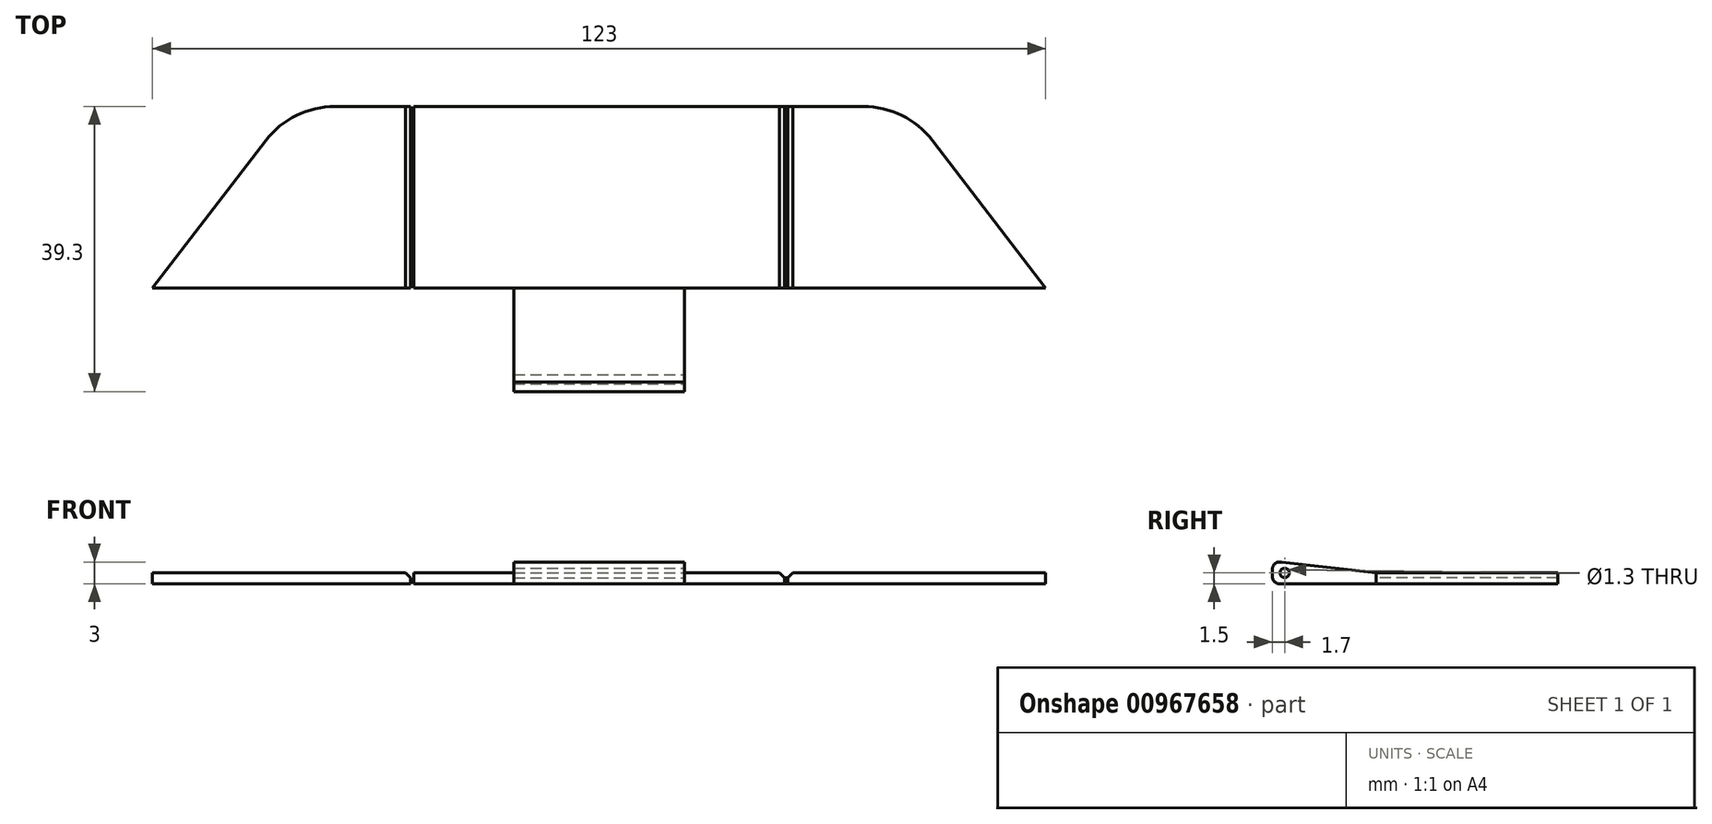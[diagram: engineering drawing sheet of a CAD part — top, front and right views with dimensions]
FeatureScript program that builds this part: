
annotation { "Feature Type Name" : "Feature", "Feature Type Description" : "" }
export const myFeature = defineFeature(function(context is Context, id is Id, definition is map)
    precondition{}
    {
        {
            var Q0;
            Q0=qCreatedBy(makeId("Top.planeOp"),FACE);
            var sketch = newSketch(context, id + "F0", { "sketchPlane" : qUnion([Q0])});
            skLineSegment(sketch, "E0.bottom", {"start": v(-11.75, -19.65) * mm, "end": v(11.75, -19.65) * mm});
            skLineSegment(sketch, "E0.top", {"start": v(-11.75, 19.65) * mm, "end": v(11.75, 19.65) * mm});
            skLineSegment(sketch, "E0.left", {"start": v(-11.75, -19.65) * mm, "end": v(-11.75, -5.35) * mm});
            skLineSegment(sketch, "E0.right", {"start": v(11.75, -19.65) * mm, "end": v(11.75, -5.35) * mm});
            skPoint(sketch, "E0.middle", {"position": v(0, 0) * mm});
            skLineSegment(sketch, "E1", {"start": v(-17.83, -17.95) * mm, "end": v(20.68, -17.95) * mm, "construction": true});
            skLineSegment(sketch, "E2", {"start": v(-16.64, -5.35) * mm, "end": v(-11.75, -5.35) * mm, "construction": true});
            skLineSegment(sketch, "E3.bottom", {"start": v(-25.5, -5.35) * mm, "end": v(-11.75, -5.35) * mm});
            skLineSegment(sketch, "E3.top", {"start": v(-25.5, 19.65) * mm, "end": v(25.5, 19.65) * mm});
            skLineSegment(sketch, "E3.left", {"start": v(-25.5, -5.35) * mm, "end": v(-25.5, 19.65) * mm});
            skLineSegment(sketch, "E3.right", {"start": v(25.5, -5.35) * mm, "end": v(25.5, 19.65) * mm});
            skPoint(sketch, "E3.middle", {"position": v(0, 7.15) * mm});
            skLineSegment(sketch, "E4.trimOffspring", {"start": v(11.75, -5.35) * mm, "end": v(19.97, -5.35) * mm, "construction": true});
            skLineSegment(sketch, "E5.trimOffspring", {"start": v(11.75, -5.35) * mm, "end": v(25.5, -5.35) * mm});
            skPoint(sketch, "E6.oppositeSnap0", {"position": v(-18.62, -5.35) * mm});
            skLineSegment(sketch, "E6.bottom", {"start": v(-25.5, 19.65) * mm, "end": v(-36.38, 19.65) * mm});
            skLineSegment(sketch, "E6.top", {"start": v(-25.5, -5.35) * mm, "end": v(-61.5, -5.35) * mm});
            skLineSegment(sketch, "E6.left", {"start": v(-25.5, 19.65) * mm, "end": v(-25.5, -5.35) * mm});
            skLineSegment(sketch, "E7", {"start": v(-26, 19.65) * mm, "end": v(-26, -5.35) * mm});
            skLineSegment(sketch, "E8", {"start": v(-45.9, 14.96) * mm, "end": v(-61.5, -5.35) * mm});
            skPoint(sketch, "E9.visualSharp", {"position": v(-42.3, 19.65) * mm});
            skArc(sketch, "E9.filletArc", {"start": v(-36.38, 19.65) * mm, "mid": v(-41.68, 18.41) * mm, "end": v(-45.9, 14.96) * mm});
            skLineSegment(sketch, "E10.MirrorCS", {"start": v(26, 19.65) * mm, "end": v(26, -5.35) * mm});
            skLineSegment(sketch, "E11.MirrorCS", {"start": v(25.5, 19.65) * mm, "end": v(36.38, 19.65) * mm});
            skArc(sketch, "E12.MirrorCS", {"start": v(36.38, 19.65) * mm, "mid": v(41.68, 18.41) * mm, "end": v(45.9, 14.96) * mm});
            skLineSegment(sketch, "E13.MirrorCS", {"start": v(45.9, 14.96) * mm, "end": v(61.5, -5.35) * mm});
            skLineSegment(sketch, "E14.MirrorCS", {"start": v(25.5, -5.35) * mm, "end": v(61.5, -5.35) * mm});
            skLineSegment(sketch, "E15", {"start": v(-11.75, -5.35) * mm, "end": v(11.75, -5.35) * mm});
            skSolve(sketch);
        }
        {
            var Q0;
            Q0=makeQuery(id+"F0.imprint","IMPRINT",FACE,{"disambiguationData":[TD([[makeQuery(id+"F0.imprint","IMPRINT",EDGE,{"derivedFrom":sQuery(id+"F0.wireOp",EDGE,"E0.bottom")}),1.0]])]});
            extrude(context, id + "F1", {"entities" : qUnion([Q0]), "depth" : 3 * mm, "offsetDistance" : 25 * mm});
        }
        {
            var Q0;
            Q0=makeQuery(id+"F1.opExtrude","SWEPT_FACE",FACE,{"disambiguationData":[OSD([sQuery(id+"F0.wireOp",EDGE,"E0.right")])]});
            var sketch = newSketch(context, id + "F2", { "sketchPlane" : qUnion([Q0])});
            skCircle(sketch, "E16", {"center": v(-17.95, 1.5) * mm, "radius": 0.65 * mm});
            skLineSegment(sketch, "E17", {"start": v(-16, 3) * mm, "end": v(-19.65, 0) * mm, "construction": true});
            skLineSegment(sketch, "E18", {"start": v(-16, 0) * mm, "end": v(-19.65, 3) * mm, "construction": true});
            skLineSegment(sketch, "E19", {"start": v(-17.82, 1.5) * mm, "end": v(-18.92, 1.5) * mm, "construction": true});
            skSolve(sketch);
        }
        {
            var Q0;
            Q0 = qSketchRegion(id + "F2", true);
            extrude(context, id + "F3", {"entities" : qUnion([Q0]), "operationType" : NewBodyOperationType.REMOVE, "oppositeDirection" : true, "depth" : 25 * mm, "offsetDistance" : 25 * mm});
        }
        {
            var Q0;
            Q0=makeQuery(id+"F1.opExtrude","CAP_EDGE",EDGE,{"disambiguationData":[OSD([sQuery(id+"F0.wireOp",EDGE,"E0.bottom")])],"isStart":false});
            var Q1;
            Q1=makeQuery(id+"F1.opExtrude","CAP_EDGE",EDGE,{"disambiguationData":[OSD([sQuery(id+"F0.wireOp",EDGE,"E0.bottom")])],"isStart":true});
            fillet(context, id + "F4", {"entities" : qUnion([Q0, Q1]), "radius" : 1 * mm, "tangentPropagation" : true, "allowEdgeOverflow" : false});
        }
        {
            var Q0;
            {var subQ0=sQuery(id+"F0.wireOp",EDGE,"E7");Q0=makeQuery(id+"F0.imprint","IMPRINT",FACE,{"disambiguationData":[TD([[makeQuery(id+"F0.imprint","IMPRINT",EDGE,{"derivedFrom":subQ0}),-1.0]])]});}
            var Q1;
            {var subQ3=sQuery(id+"F0.wireOp",EDGE,"E10.MirrorCS");Q1=makeQuery(id+"F0.imprint","IMPRINT",FACE,{"disambiguationData":[TD([[makeQuery(id+"F0.imprint","IMPRINT",EDGE,{"derivedFrom":subQ3}),1.0]])]});}
            extrude(context, id + "F5", {"entities" : qUnion([Q0, Q1]), "depth" : 1.5 * mm, "offsetDistance" : 25 * mm});
        }
        {
            var Q0;
            {var subQ0=sQuery(id+"F0.wireOp",EDGE,"E6.left");Q0=makeQuery(id+"F0.imprint","IMPRINT",FACE,{"disambiguationData":[TD([[makeQuery(id+"F0.imprint","IMPRINT",EDGE,{"derivedFrom":subQ0}),-1.0]])]});}
            var Q1;
            {var subQ0=sQuery(id+"F0.wireOp",EDGE,"E3.right");Q1=makeQuery(id+"F0.imprint","IMPRINT",FACE,{"disambiguationData":[TD([[makeQuery(id+"F0.imprint","IMPRINT",EDGE,{"derivedFrom":subQ0}),-1.0]])]});}
            extrude(context, id + "F6", {"entities" : qUnion([Q0, Q1]), "depth" : .8 * mm, "offsetDistance" : 25 * mm});
        }
        {
            var Q0;
            Q0=makeQuery(id+"F0.imprint","IMPRINT",FACE,{"disambiguationData":[TD([[makeQuery(id+"F0.imprint","IMPRINT",EDGE,{"derivedFrom":sQuery(id+"F0.wireOp",EDGE,"E3.bottom")}),1.0]])]});
            extrude(context, id + "F7", {"entities" : qUnion([Q0]), "depth" : 1.5 * mm, "offsetDistance" : 25 * mm});
        }
        {
            var Q0;
            Q0=makeQuery(id+"F7.opExtrude","CAP_EDGE",EDGE,{"disambiguationData":[OSD([sQuery(id+"F0.wireOp",EDGE,"E6.left")])],"isStart":false});
            var Q1;
            Q1=makeQuery(id+"F5.opExtrude","CAP_EDGE",EDGE,{"disambiguationData":[OSD([sQuery(id+"F0.wireOp",EDGE,"E7")])],"isStart":false});
            var Q2;
            Q2=makeQuery(id+"F5.opExtrude","CAP_EDGE",EDGE,{"disambiguationData":[OSD([sQuery(id+"F0.wireOp",EDGE,"E10.MirrorCS")])],"isStart":false});
            var Q3;
            Q3=makeQuery(id+"F7.opExtrude","CAP_EDGE",EDGE,{"disambiguationData":[OSD([sQuery(id+"F0.wireOp",EDGE,"E3.right")])],"isStart":false});
            chamfer(context, id + "F8", {"entities" : qUnion([Q0, Q1, Q2, Q3]), "width" : .7 * mm, "tangentPropagation" : true});
        }
        {
            var Q0;
            Q0=makeQuery(id+"F1.opExtrude","CAP_EDGE",EDGE,{"disambiguationData":[OSD([sQuery(id+"F0.wireOp",EDGE,"E15")])],"isStart":false});
            chamfer(context, id + "F9", {"entities" : qUnion([Q0]), "chamferType" : ChamferType.TWO_OFFSETS, "width1" : 1.5 * mm, "oppositeDirection" : false, "width2" : 13 * mm, "tangentPropagation" : true});
        }
    });
